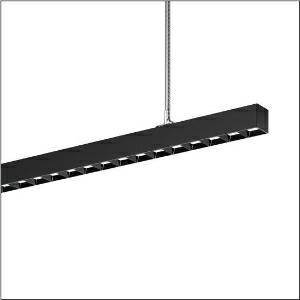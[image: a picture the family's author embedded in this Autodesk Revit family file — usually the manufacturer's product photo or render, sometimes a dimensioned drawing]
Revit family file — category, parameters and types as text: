
# Revit family: silica_21_51mx32dc4dbb
name_source: partatom
category: Lighting Fixtures
units: mm (PartAtom-declared; Revit-internal decimal feet)

## family parameters
Cut with Voids When Loaded = No
Host = Face
Light Source = No
Part Type = Normal
Room Calculation Point = No
Round Connector Dimension = Use Diameter
Shared = No

## types (1)
- --- (1 x LED, 18230 lm, 105.8 W, 4000K)
    Apparent Load = 106 VA
    CIE Flux Codes = 86 99 100 59 100
    Color Rendering = 80
    Color Temperature = 4000K
    Default Elevation = 1800 mm
    Description = Silica 21, office luminaire, primary light control with darklight reflector, of PMMA, black, CAT 2 (L<= 3000cd/m²), light emission: direct/indirect distribution, primary light characteristic: symmetric, installation type: suspended mounting, LED, rated luminous flux: 18.230lm, luminous efficacy: 172lm/W, light colour: 840, colour temperature: 4000K, control gear: DALI 2, with terminal, 3+2-pole, max. 2.5mm², mains connection: 220..240V, AC, 50/60Hz, rated input power: 105.8W, luminaire housing, of aluminium, matt jet black (RAL 9005), length: 3.004mm, width: 53mm, height: 53mm, protection rating (complete): IP20, insulation class (complete): insulation class I (protective earthing), certification: CE, permissible operating ambient temperature: 0..+35°C, standard: EN 50419, packaging unit: 1 piece
    Height = 53 mm
    Lamp = 1 x LED
    Lamp Light Flux = 18230 lm
    Lamp Power = 105.8 W
    Lamp count = 1
    Length = 3004 mm
    Luminous efficacy = 172 lm/W
    Manufacturer = Siteco
    ModVariant = No
    Model = 51MX32DC4DBB
    Mounting Place = Ceiling
    Mounting Type = Pendant
    Number of Poles = 1
    OnlyDefault = Yes
    Power Factor = 1
    Product Name = Silica 21
    Product group = office luminaire | ceiling pendant
    ProductGroupID = 903
    Protection Class = Protection class I
    Protection Degree = IP 20
    RLX_Detail_Level = 1
    RLX_Emergency_Light_Flux = 0 lm
    RLX_Emergency_Type = 0
    RLX_Emergency_Type_DB = No
    RlxData = <blob elided: 69633 chars, md5=0ee1b6dd>
    Socket = socket
    Standby Power = 0 W
    System Light Flux = 18230 lm
    System Power = 106 W
    Type Comments = factory setting: luminous flux: 100 % | dim-lin: 254 | 366 mA
    Type Image = l_1335852.jpg
    URL = http://relux.com
    VarID = @adj_122277
    Voltage = 0 V
    Weight = 0.00 kg
    Width = 53 mm

## geometry (parser evidence)
native form markers: Blend x4, Sweep x13
no freeform markers — native parametric forms only
